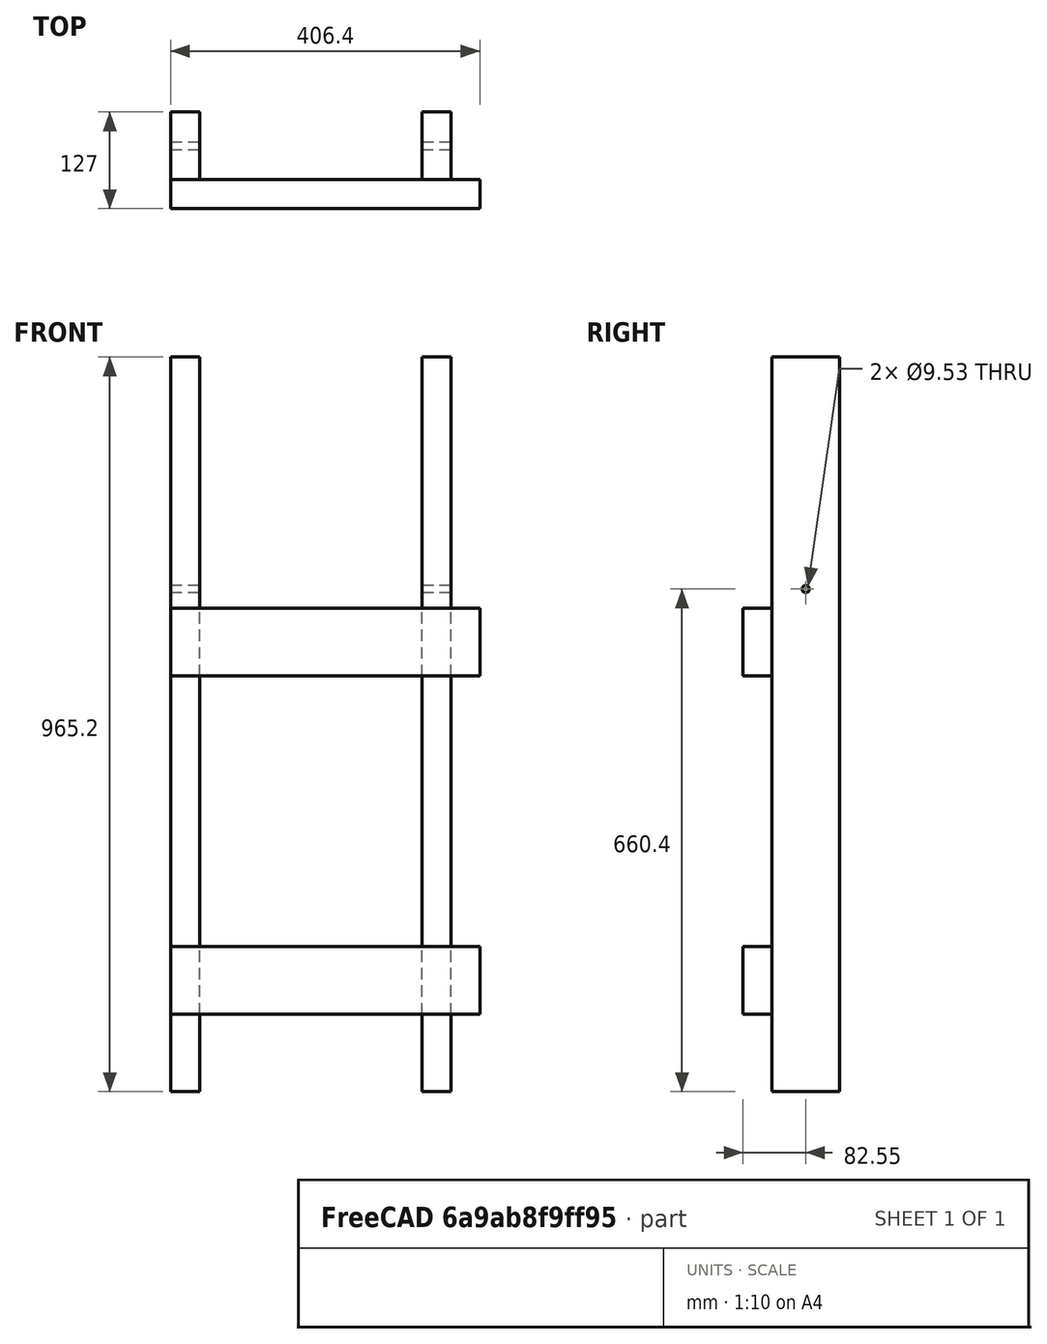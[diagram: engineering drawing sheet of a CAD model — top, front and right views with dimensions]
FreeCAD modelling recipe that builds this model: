
FCSTD DOCUMENT  (FreeCAD 0.21R33771 (Git))
Label: MastHorse
License: All rights reserved
LicenseURL: http://en.wikipedia.org/wiki/All_rights_reserved
objects: TechDraw::DrawViewDimension×7, Sketcher::SketchObject×4, TechDraw::DrawViewPart×3, Part::Extrusion×2, PartDesign::FeatureBase×2, PartDesign::Pocket×2, PartDesign::Body×2, TechDraw::DrawSVGTemplate×1, TechDraw::DrawPage×1
note: 27 computed .brp shape members not serialized (recipe doc carries the construction recipe); baked Part::Feature solids carry a one-line shape summary decoded from their .brp

FEATURE [Sketcher::SketchObject] Sketch
  FullyConstrained = true
  MapMode = 2
  Support = -> [Sketch]
  sketch-geometry (4):
    g0: LineSegment StartX=0 StartY=0 StartZ=0 EndX=38.1 EndY=0 EndZ=0
    g1: LineSegment StartX=38.1 StartY=0 StartZ=0 EndX=38.1 EndY=88.9 EndZ=0
    g2: LineSegment StartX=38.1 StartY=88.9 StartZ=0 EndX=0 EndY=88.9 EndZ=0
    g3: LineSegment StartX=0 StartY=88.9 StartZ=0 EndX=0 EndY=0 EndZ=0
  constraints (11):
    c: Coincident(g0,g-1)
    c: Coincident(g1,g0)
    c: Vertical(g1)
    c: Coincident(g2,g1)
    c: Horizontal(g2)
    c: Coincident(g3,g2)
    c: Coincident(g3,g0)
    c: Vertical(g3)
    c: Horizontal(g0)
    c: DistanceX(g3,g1) = 38.1
    c: DistanceY(g3,g2) = 88.9
FEATURE [Sketcher::SketchObject] Sketch001
  FullyConstrained = true
  sketch-geometry (4):
    g0: LineSegment StartX=0 StartY=0 StartZ=0 EndX=406.4 EndY=0 EndZ=0
    g1: LineSegment StartX=406.4 StartY=0 StartZ=0 EndX=406.4 EndY=-38.1 EndZ=0
    g2: LineSegment StartX=406.4 StartY=-38.1 StartZ=0 EndX=0 EndY=-38.1 EndZ=0
    g3: LineSegment StartX=0 StartY=-38.1 StartZ=0 EndX=0 EndY=0 EndZ=0
  constraints (11):
    c: Coincident(g0,g-1)
    c: Horizontal(g0)
    c: Coincident(g1,g0)
    c: Vertical(g1)
    c: Coincident(g2,g1)
    c: Horizontal(g2)
    c: Coincident(g3,g2)
    c: Coincident(g3,g0)
    c: Vertical(g3)
    c: DistanceX(g0,g0) = 406.4
    c: DistanceY(g2,g0) = 38.1
FEATURE [Part::Extrusion] Extrude002  label="Rung 1"
  Base = -> Sketch001
  Dir = (0,0,1)
  DirMode = 2
  FaceMakerClass = Part::FaceMakerBullseye
  LengthFwd = 88.9
  LengthRev = 0
  Placement = pos=(0,0,101.6) rot=(0,0,1;0rad)
  Solid = true
  Symmetric = false
FEATURE [Sketcher::SketchObject] Sketch002
  FullyConstrained = true
  sketch-geometry (4):
    g0: LineSegment StartX=0 StartY=0 StartZ=0 EndX=406.4 EndY=0 EndZ=0
    g1: LineSegment StartX=406.4 StartY=0 StartZ=0 EndX=406.4 EndY=-38.1 EndZ=0
    g2: LineSegment StartX=406.4 StartY=-38.1 StartZ=0 EndX=0 EndY=-38.1 EndZ=0
    g3: LineSegment StartX=0 StartY=-38.1 StartZ=0 EndX=0 EndY=0 EndZ=0
  constraints (11):
    c: Coincident(g0,g-1)
    c: Horizontal(g0)
    c: Coincident(g1,g0)
    c: Vertical(g1)
    c: Coincident(g2,g1)
    c: Horizontal(g2)
    c: Coincident(g3,g2)
    c: Coincident(g3,g0)
    c: Vertical(g3)
    c: DistanceX(g0,g0) = 406.4
    c: DistanceY(g2,g0) = 38.1
FEATURE [Part::Extrusion] Extrude003  label="Rung 2"
  Base = -> Sketch002
  Dir = (0,0,1)
  DirMode = 2
  FaceMakerClass = Part::FaceMakerBullseye
  LengthFwd = 88.9
  LengthRev = 0
  Placement = pos=(0,0,546.1) rot=(0,0,1;0rad)
  Solid = true
  Symmetric = false
FEATURE [PartDesign::FeatureBase] BaseFeature
FEATURE [Sketcher::SketchObject] Sketch003
  FullyConstrained = true
  MapMode = 5
  Placement = pos=(0,0,0) rot=(0.57735,-0.57735,-0.57735;2.0944rad)
  Support = -> [BaseFeature]
  sketch-geometry (1):
    g0: Circle CenterX=-44.45 CenterY=660.4 CenterZ=0 NormalX=0 NormalY=0 NormalZ=1 AngleXU=0 Radius=4.7625
  constraints (3):
    c: DistanceX(g0,g-1) = 44.45
    c: DistanceY(g-1,g0) = 660.4
    c: Diameter(g0) = 9.525
FEATURE [PartDesign::Pocket] Pocket
  BaseFeature = -> BaseFeature
  Direction = (1,0,0)
  Length = 76.2
  Length2 = 5
  Profile = -> Sketch003
  ReferenceAxis = -> Sketch003 [N_Axis]
  Type = 1
FEATURE [PartDesign::Body] Body
  Group = -> [BaseFeature,Sketch003,Pocket]
  Origin = -> Origin
  Tip = -> Pocket
FEATURE [PartDesign::Pocket] Pocket001
  BaseFeature = -> BaseFeature
  Direction = (1,0,0)
  Length = 76.2
  Length2 = 5
  Profile = -> Sketch003
  ReferenceAxis = -> Sketch003 [N_Axis]
  Type = 1
FEATURE [PartDesign::FeatureBase] BaseFeature001
  BaseFeature = -> Pocket001
FEATURE [PartDesign::Body] Body001
  BaseFeature = -> Pocket001
  Group = -> [BaseFeature001]
  Origin = -> Origin001
  Placement = pos=(330.2,0,0) rot=(0,0,1;0rad)
  Tip = -> BaseFeature001
FEATURE [TechDraw::DrawSVGTemplate] Template001
  EditableTexts = AUTHOR_NAME=David Numan; DRAWING_TITLE=Mast Horse; FC-DATE=26/12/2023; FC-REV=REV A; FC-SC=SCALE; FC-SH=X / Y; FC-SI=A4; SI-2=Two of these are required for one mast horse.; SI-4=The diameter of the holes should match the selected; SI-5=bolt hardware
  Height = 297
  Orientation = 0
  Template = <path>
  Width = 210
FEATURE [TechDraw::DrawViewPart] View  label="Front"
  CoarseView = false
  Direction = (0,-1,0)
  Focus = 100
  HardHidden = false
  IsoCount = 0
  IsoHidden = false
  IsoVisible = false
  LockPosition = false
  Perspective = false
  Rotation = 0
  Scale = 0.125
  ScaleType = 0
  ScrubCount = 0
  SeamHidden = false
  SeamVisible = true
  SmoothHidden = false
  SmoothVisible = true
  Source = -> [Pocket001,Sketch,Extrude002,Extrude003,Body,Body001,Origin,BaseFeature,Pocket,Sketch003]
  X = 52.1957
  XDirection = (1,0,0)
  Y = 203.43
FEATURE [TechDraw::DrawViewPart] View001  label="Side"
  CoarseView = false
  Direction = (1,0,0)
  Focus = 100
  HardHidden = false
  IsoCount = 0
  IsoHidden = false
  IsoVisible = false
  LockPosition = false
  Perspective = false
  Rotation = 0
  Scale = 0.125
  ScaleType = 0
  ScrubCount = 0
  SeamHidden = false
  SeamVisible = true
  SmoothHidden = false
  SmoothVisible = true
  Source = -> [Pocket001,Sketch,Extrude002,Extrude003,Body,Body001,Origin,BaseFeature,Pocket,Sketch003]
  X = 174.052
  XDirection = (0,1,0)
  Y = 217.846
FEATURE [TechDraw::DrawViewPart] View002
  CoarseView = false
  Direction = (0.57735,-0.57735,0.57735)
  Focus = 100
  HardHidden = false
  IsoCount = 0
  IsoHidden = false
  IsoVisible = true
  LockPosition = false
  Perspective = false
  Rotation = 0
  Scale = 0.125
  ScaleType = 0
  ScrubCount = 0
  SeamHidden = false
  SeamVisible = true
  SmoothHidden = false
  SmoothVisible = false
  Source = -> [Pocket001,Sketch,Extrude002,Extrude003,Body,Body001,Origin,BaseFeature,Pocket,Sketch003]
  X = 118.119
  XDirection = (0.707107,0.707107,0)
  Y = 133.131
FEATURE [TechDraw::DrawViewDimension] Dimension
  AngleOverride = false
  Arbitrary = false
  ArbitraryTolerances = false
  EqualTolerance = true
  ExtensionAngle = 0
  FormatSpec = ⌀%.2w
  FormatSpecOverTolerance = %+.2w
  FormatSpecUnderTolerance = %+.2w
  Inverted = false
  LineAngle = 0
  LockPosition = false
  MeasureType = 1
  OverTolerance = 0
  References2D = -> [View001]
  Rotation = 0
  Scale = 0.125
  ScaleType = 0
  TheoreticalExact = false
  Type = 5
  UnderTolerance = 0
  X = -19.5204
  Y = 44.6459
FEATURE [TechDraw::DrawViewDimension] Dimension001
  AngleOverride = false
  Arbitrary = false
  ArbitraryTolerances = false
  EqualTolerance = true
  ExtensionAngle = 0
  FormatSpec = %.2w
  FormatSpecOverTolerance = %+.2w
  FormatSpecUnderTolerance = %+.2w
  Inverted = false
  LineAngle = 0
  LockPosition = false
  MeasureType = 1
  OverTolerance = 0
  References2D = -> [View]
  Rotation = 0
  Scale = 0.125
  ScaleType = 0
  TheoreticalExact = false
  Type = 2
  UnderTolerance = 0
  X = 27.5937
  Y = -12.3255
FEATURE [TechDraw::DrawViewDimension] Dimension003
  AngleOverride = false
  Arbitrary = false
  ArbitraryTolerances = false
  EqualTolerance = true
  ExtensionAngle = 0
  FormatSpec = %.2w
  FormatSpecOverTolerance = %+.2w
  FormatSpecUnderTolerance = %+.2w
  Inverted = false
  LineAngle = 0
  LockPosition = false
  MeasureType = 1
  OverTolerance = 0
  References2D = -> [View001]
  Rotation = 0
  Scale = 0.125
  ScaleType = 0
  TheoreticalExact = false
  Type = 2
  UnderTolerance = 0
  X = -17.1664
  Y = -48.8404
FEATURE [TechDraw::DrawViewDimension] Dimension004
  AngleOverride = false
  Arbitrary = false
  ArbitraryTolerances = false
  EqualTolerance = true
  ExtensionAngle = 0
  FormatSpec = %.2w
  FormatSpecOverTolerance = %+.2w
  FormatSpecUnderTolerance = %+.2w
  Inverted = false
  LineAngle = 0
  LockPosition = false
  MeasureType = 1
  OverTolerance = 0
  References2D = -> [View]
  Rotation = 0
  Scale = 0.125
  ScaleType = 0
  TheoreticalExact = false
  Type = 1
  UnderTolerance = 0
  X = -0.005971
  Y = 79.0985
FEATURE [TechDraw::DrawViewDimension] Dimension005
  AngleOverride = false
  Arbitrary = false
  ArbitraryTolerances = false
  EqualTolerance = true
  ExtensionAngle = 0
  FormatSpec = %.2w
  FormatSpecOverTolerance = %+.2w
  FormatSpecUnderTolerance = %+.2w
  Inverted = false
  LineAngle = 0
  LockPosition = false
  MeasureType = 1
  OverTolerance = 0
  References2D = -> [View]
  Rotation = 0
  Scale = 0.125
  ScaleType = 0
  TheoreticalExact = false
  Type = 1
  UnderTolerance = 0
  X = 1.27848
  Y = -60.1688
FEATURE [TechDraw::DrawViewDimension] Dimension006
  AngleOverride = false
  Arbitrary = false
  ArbitraryTolerances = false
  EqualTolerance = true
  ExtensionAngle = 0
  FormatSpec = %.2w
  FormatSpecOverTolerance = %+.2w
  FormatSpecUnderTolerance = %+.2w
  Inverted = false
  LineAngle = 0
  LockPosition = false
  MeasureType = 1
  OverTolerance = 0
  References2D = -> [View001]
  Rotation = 0
  Scale = 0.125
  ScaleType = 0
  TheoreticalExact = false
  Type = 2
  UnderTolerance = 0
  X = -28.2702
  Y = -18.6402
FEATURE [TechDraw::DrawViewDimension] Dimension007
  AngleOverride = false
  Arbitrary = false
  ArbitraryTolerances = false
  EqualTolerance = true
  ExtensionAngle = 0
  FormatSpec = %.2w
  FormatSpecOverTolerance = %+.2w
  FormatSpecUnderTolerance = %+.2w
  Inverted = false
  LineAngle = 0
  LockPosition = false
  MeasureType = 1
  OverTolerance = 0
  References2D = -> [View001]
  Rotation = 0
  Scale = 0.125
  ScaleType = 0
  TheoreticalExact = false
  Type = 2
  UnderTolerance = 0
  X = 15.7275
  Y = 0.176741
FEATURE [TechDraw::DrawPage] Page001
  KeepUpdated = true
  NextBalloonIndex = 1
  ProjectionType = 0
  Scale = 0.125
  Template = -> Template001
  Views = -> [View,View001,View002,Dimension,Dimension001,Dimension003,Dimension004,Dimension005,Dimension006,Dimension007]
note: 1 file-system path scrubbed to <path> (originals preserved in the JSON sidecar)
